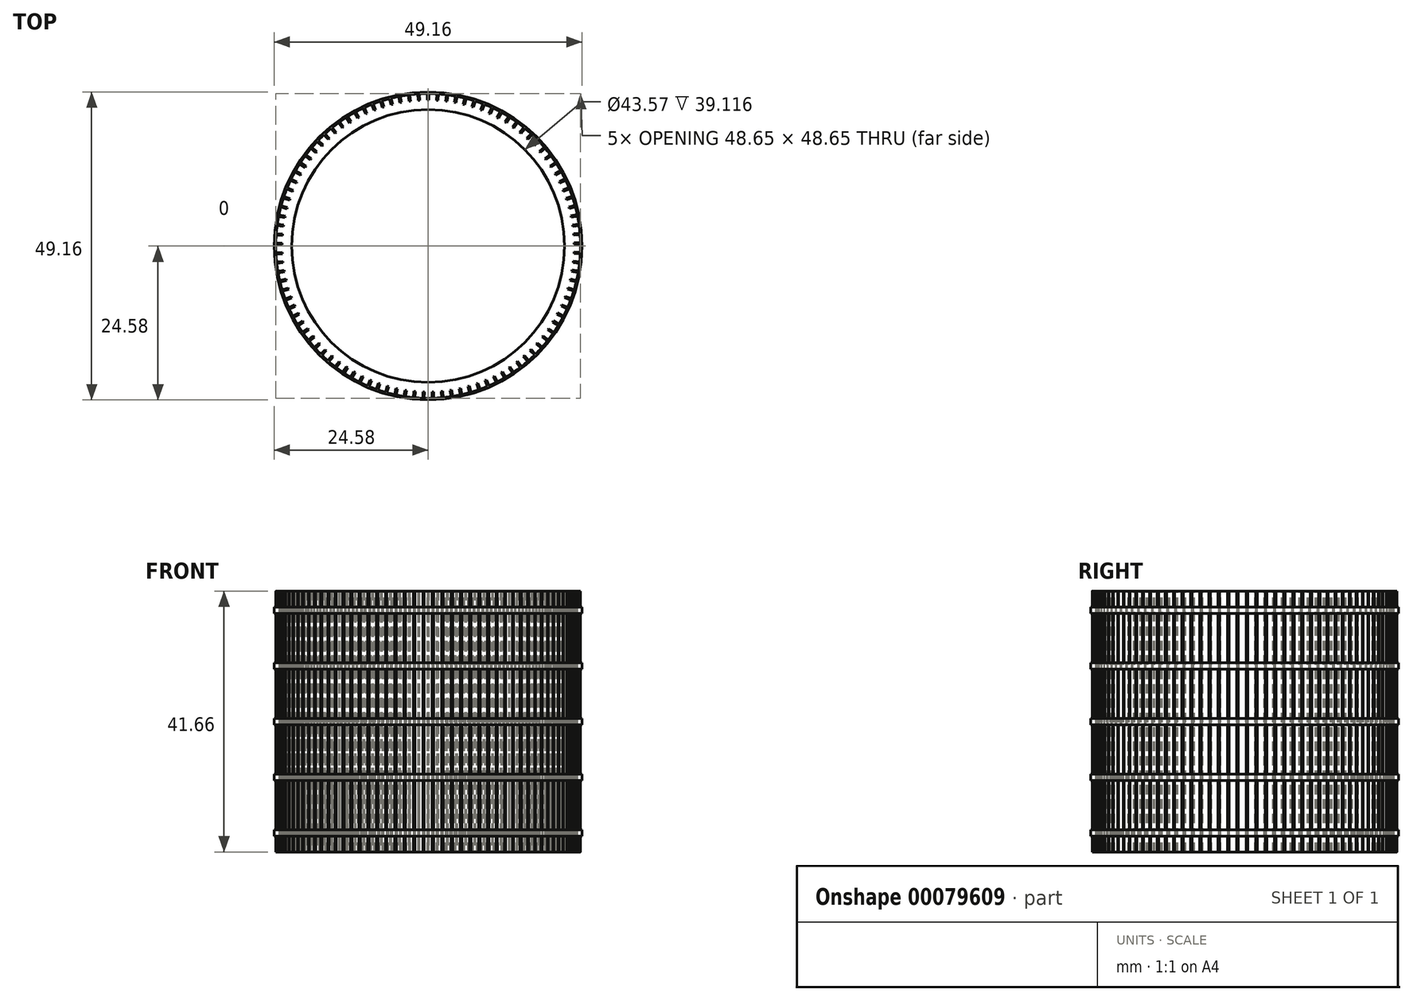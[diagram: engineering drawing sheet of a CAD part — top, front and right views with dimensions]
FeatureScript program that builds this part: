
annotation { "Feature Type Name" : "Feature", "Feature Type Description" : "" }
export const myFeature = defineFeature(function(context is Context, id is Id, definition is map)
    precondition{}
    {
        {
            var Q0;
            Q0=qCreatedBy(makeId("Top.planeOp"),FACE);
            var sketch = newSketch(context, id + "F0", { "sketchPlane" : qUnion([Q0])});
            skCircle(sketch, "E0", {"center": v(0, 0) * mm, "radius": 24.32 * mm});
            skSolve(sketch);
        }
        {
            var Q0;
            Q0=qCreatedBy(makeId("Top.planeOp"),FACE);
            cPlane(context, id + "F1", {"entities" : qUnion([Q0]), "cplaneType" : CPlaneType.OFFSET, "offset" : 2.54 * mm, "width" : 152.4 * mm, "height" : 152.4 * mm});
        }
        {
            var Q0;
            Q0=qCreatedBy(id+"F1.planeOp",FACE);
            cPlane(context, id + "F2", {"entities" : qUnion([Q0]), "cplaneType" : CPlaneType.OFFSET, "offset" : 8.9 * mm, "width" : 152.4 * mm, "height" : 152.4 * mm});
        }
        {
            var Q0;
            Q0=qCreatedBy(id+"F2.planeOp",FACE);
            cPlane(context, id + "F3", {"entities" : qUnion([Q0]), "cplaneType" : CPlaneType.OFFSET, "offset" : 8.9 * mm, "width" : 152.4 * mm, "height" : 152.4 * mm});
        }
        {
            var Q0;
            Q0=qCreatedBy(id+"F3.planeOp",FACE);
            cPlane(context, id + "F4", {"entities" : qUnion([Q0]), "cplaneType" : CPlaneType.OFFSET, "offset" : 8.9 * mm, "width" : 152.4 * mm, "height" : 152.4 * mm});
        }
        {
            var Q0;
            Q0=qSketchRegion(id+"F0",true);
            extrude(context, id + "F5", {"entities" : qUnion([Q0]), "depth" : 41.66 * mm});
        }
        {
            var Q0;
            Q0=makeQuery(id+"F5.opExtrude","CAP_FACE",FACE,{"disambiguationData":[OSD([sQuery(id+"F0.wireOp",EDGE,"E0")])],"isStart":false});
            shell(context, id + "F6", {"entities" : qUnion([Q0]), "thickness" : 2.54 * mm});
        }
        {
            var Q0;
            Q0=makeQuery(id+"F5.opExtrude","CAP_FACE",FACE,{"disambiguationData":[OSD([sQuery(id+"F0.wireOp",EDGE,"E0")])],"isStart":false});
            var sketch = newSketch(context, id + "F7", { "sketchPlane" : qUnion([Q0])});
            skLineSegment(sketch, "E1.left", {"start": v(-0.13, 24.61) * mm, "end": v(-0.13, 23.3) * mm});
            skLineSegment(sketch, "E1.right", {"start": v(0.13, 24.61) * mm, "end": v(0.13, 23.3) * mm});
            skLineSegment(sketch, "E2.1.0", {"start": v(1.4, 24.57) * mm, "end": v(1.32, 23.27) * mm});
            skLineSegment(sketch, "E2.1.1", {"start": v(1.66, 24.56) * mm, "end": v(1.58, 23.25) * mm});
            skLineSegment(sketch, "E2.1.2", {"start": v(1.32, 23.27) * mm, "end": v(1.58, 23.25) * mm});
            skLineSegment(sketch, "E2.1.3", {"start": v(1.4, 24.57) * mm, "end": v(1.66, 24.56) * mm});
            skLineSegment(sketch, "E2.2.0", {"start": v(2.93, 24.44) * mm, "end": v(2.77, 23.14) * mm});
            skLineSegment(sketch, "E2.2.1", {"start": v(3.18, 24.4) * mm, "end": v(3.02, 23.11) * mm});
            skLineSegment(sketch, "E2.2.2", {"start": v(2.77, 23.14) * mm, "end": v(3.02, 23.11) * mm});
            skLineSegment(sketch, "E2.2.3", {"start": v(2.93, 24.44) * mm, "end": v(3.18, 24.4) * mm});
            skLineSegment(sketch, "E2.3.0", {"start": v(4.44, 24.21) * mm, "end": v(4.2, 22.93) * mm});
            skLineSegment(sketch, "E2.3.1", {"start": v(4.7, 24.16) * mm, "end": v(4.45, 22.88) * mm});
            skLineSegment(sketch, "E2.3.2", {"start": v(4.2, 22.93) * mm, "end": v(4.45, 22.88) * mm});
            skLineSegment(sketch, "E2.3.3", {"start": v(4.44, 24.21) * mm, "end": v(4.7, 24.16) * mm});
            skLineSegment(sketch, "E2.4.0", {"start": v(5.94, 23.89) * mm, "end": v(5.62, 22.62) * mm});
            skLineSegment(sketch, "E2.4.1", {"start": v(6.18, 23.83) * mm, "end": v(5.86, 22.56) * mm});
            skLineSegment(sketch, "E2.4.2", {"start": v(5.62, 22.62) * mm, "end": v(5.86, 22.56) * mm});
            skLineSegment(sketch, "E2.4.3", {"start": v(5.94, 23.89) * mm, "end": v(6.18, 23.83) * mm});
            skLineSegment(sketch, "E2.5.0", {"start": v(7.41, 23.47) * mm, "end": v(7.01, 22.23) * mm});
            skLineSegment(sketch, "E2.5.1", {"start": v(7.65, 23.4) * mm, "end": v(7.25, 22.15) * mm});
            skLineSegment(sketch, "E2.5.2", {"start": v(7.01, 22.23) * mm, "end": v(7.25, 22.15) * mm});
            skLineSegment(sketch, "E2.5.3", {"start": v(7.41, 23.47) * mm, "end": v(7.65, 23.4) * mm});
            skLineSegment(sketch, "E2.6.0", {"start": v(8.85, 22.97) * mm, "end": v(8.38, 21.75) * mm});
            skLineSegment(sketch, "E2.6.1", {"start": v(9.1, 22.87) * mm, "end": v(8.61, 21.66) * mm});
            skLineSegment(sketch, "E2.6.2", {"start": v(8.38, 21.75) * mm, "end": v(8.61, 21.66) * mm});
            skLineSegment(sketch, "E2.6.3", {"start": v(8.85, 22.97) * mm, "end": v(9.1, 22.87) * mm});
            skLineSegment(sketch, "E2.7.0", {"start": v(10.27, 22.37) * mm, "end": v(9.71, 21.19) * mm});
            skLineSegment(sketch, "E2.7.1", {"start": v(10.5, 22.26) * mm, "end": v(9.94, 21.08) * mm});
            skLineSegment(sketch, "E2.7.2", {"start": v(9.71, 21.19) * mm, "end": v(9.94, 21.08) * mm});
            skLineSegment(sketch, "E2.7.3", {"start": v(10.27, 22.37) * mm, "end": v(10.5, 22.26) * mm});
            skLineSegment(sketch, "E2.8.0", {"start": v(11.64, 21.7) * mm, "end": v(11.01, 20.54) * mm});
            skLineSegment(sketch, "E2.8.1", {"start": v(11.86, 21.57) * mm, "end": v(11.24, 20.42) * mm});
            skLineSegment(sketch, "E2.8.2", {"start": v(11.01, 20.54) * mm, "end": v(11.24, 20.42) * mm});
            skLineSegment(sketch, "E2.8.3", {"start": v(11.64, 21.7) * mm, "end": v(11.86, 21.57) * mm});
            skLineSegment(sketch, "E2.9.0", {"start": v(12.96, 20.93) * mm, "end": v(12.27, 19.82) * mm});
            skLineSegment(sketch, "E2.9.1", {"start": v(13.18, 20.8) * mm, "end": v(12.48, 19.68) * mm});
            skLineSegment(sketch, "E2.9.2", {"start": v(12.27, 19.82) * mm, "end": v(12.48, 19.68) * mm});
            skLineSegment(sketch, "E2.9.3", {"start": v(12.96, 20.93) * mm, "end": v(13.18, 20.8) * mm});
            skLineSegment(sketch, "E2.10.0", {"start": v(14.24, 20.08) * mm, "end": v(13.48, 19.02) * mm});
            skLineSegment(sketch, "E2.10.1", {"start": v(14.44, 19.93) * mm, "end": v(13.68, 18.87) * mm});
            skLineSegment(sketch, "E2.10.2", {"start": v(13.48, 19.02) * mm, "end": v(13.68, 18.87) * mm});
            skLineSegment(sketch, "E2.10.3", {"start": v(14.24, 20.08) * mm, "end": v(14.44, 19.93) * mm});
            skLineSegment(sketch, "E2.11.0", {"start": v(15.46, 19.16) * mm, "end": v(14.63, 18.14) * mm});
            skLineSegment(sketch, "E2.11.1", {"start": v(15.65, 19) * mm, "end": v(14.83, 17.98) * mm});
            skLineSegment(sketch, "E2.11.2", {"start": v(14.63, 18.14) * mm, "end": v(14.83, 17.98) * mm});
            skLineSegment(sketch, "E2.11.3", {"start": v(15.46, 19.16) * mm, "end": v(15.65, 19) * mm});
            skLineSegment(sketch, "E2.12.0", {"start": v(16.62, 18.16) * mm, "end": v(15.73, 17.2) * mm});
            skLineSegment(sketch, "E2.12.1", {"start": v(16.8, 17.99) * mm, "end": v(15.92, 17.03) * mm});
            skLineSegment(sketch, "E2.12.2", {"start": v(15.73, 17.2) * mm, "end": v(15.92, 17.03) * mm});
            skLineSegment(sketch, "E2.12.3", {"start": v(16.62, 18.16) * mm, "end": v(16.8, 17.99) * mm});
            skLineSegment(sketch, "E2.13.0", {"start": v(17.71, 17.1) * mm, "end": v(16.77, 16.19) * mm});
            skLineSegment(sketch, "E2.13.1", {"start": v(17.9, 16.9) * mm, "end": v(16.94, 16) * mm});
            skLineSegment(sketch, "E2.13.2", {"start": v(16.77, 16.19) * mm, "end": v(16.94, 16) * mm});
            skLineSegment(sketch, "E2.13.3", {"start": v(17.71, 17.1) * mm, "end": v(17.9, 16.9) * mm});
            skLineSegment(sketch, "E2.14.0", {"start": v(18.74, 15.96) * mm, "end": v(17.74, 15.11) * mm});
            skLineSegment(sketch, "E2.14.1", {"start": v(18.9, 15.76) * mm, "end": v(17.9, 14.92) * mm});
            skLineSegment(sketch, "E2.14.2", {"start": v(17.74, 15.11) * mm, "end": v(17.9, 14.92) * mm});
            skLineSegment(sketch, "E2.14.3", {"start": v(18.74, 15.96) * mm, "end": v(18.9, 15.76) * mm});
            skLineSegment(sketch, "E2.15.0", {"start": v(19.7, 14.76) * mm, "end": v(18.65, 13.98) * mm});
            skLineSegment(sketch, "E2.15.1", {"start": v(19.85, 14.56) * mm, "end": v(18.8, 13.78) * mm});
            skLineSegment(sketch, "E2.15.2", {"start": v(18.65, 13.98) * mm, "end": v(18.8, 13.78) * mm});
            skLineSegment(sketch, "E2.15.3", {"start": v(19.7, 14.76) * mm, "end": v(19.85, 14.56) * mm});
            skLineSegment(sketch, "E2.16.0", {"start": v(20.58, 13.5) * mm, "end": v(19.48, 12.8) * mm});
            skLineSegment(sketch, "E2.16.1", {"start": v(20.72, 13.3) * mm, "end": v(19.62, 12.58) * mm});
            skLineSegment(sketch, "E2.16.2", {"start": v(19.48, 12.8) * mm, "end": v(19.62, 12.58) * mm});
            skLineSegment(sketch, "E2.16.3", {"start": v(20.58, 13.5) * mm, "end": v(20.72, 13.3) * mm});
            skLineSegment(sketch, "E2.17.0", {"start": v(21.38, 12.2) * mm, "end": v(20.24, 11.56) * mm});
            skLineSegment(sketch, "E2.17.1", {"start": v(21.5, 11.98) * mm, "end": v(20.36, 11.34) * mm});
            skLineSegment(sketch, "E2.17.2", {"start": v(20.24, 11.56) * mm, "end": v(20.36, 11.34) * mm});
            skLineSegment(sketch, "E2.17.3", {"start": v(21.38, 12.2) * mm, "end": v(21.5, 11.98) * mm});
            skLineSegment(sketch, "E2.18.0", {"start": v(22.1, 10.85) * mm, "end": v(20.92, 10.28) * mm});
            skLineSegment(sketch, "E2.18.1", {"start": v(22.2, 10.62) * mm, "end": v(21.03, 10.05) * mm});
            skLineSegment(sketch, "E2.18.2", {"start": v(20.92, 10.28) * mm, "end": v(21.03, 10.05) * mm});
            skLineSegment(sketch, "E2.18.3", {"start": v(22.1, 10.85) * mm, "end": v(22.2, 10.62) * mm});
            skLineSegment(sketch, "E2.19.0", {"start": v(22.73, 9.46) * mm, "end": v(21.52, 8.96) * mm});
            skLineSegment(sketch, "E2.19.1", {"start": v(22.82, 9.22) * mm, "end": v(21.61, 8.73) * mm});
            skLineSegment(sketch, "E2.19.2", {"start": v(21.52, 8.96) * mm, "end": v(21.61, 8.73) * mm});
            skLineSegment(sketch, "E2.19.3", {"start": v(22.73, 9.46) * mm, "end": v(22.82, 9.22) * mm});
            skLineSegment(sketch, "E2.20.0", {"start": v(23.27, 8.03) * mm, "end": v(22.03, 7.6) * mm});
            skLineSegment(sketch, "E2.20.1", {"start": v(23.35, 7.78) * mm, "end": v(22.11, 7.36) * mm});
            skLineSegment(sketch, "E2.20.2", {"start": v(22.03, 7.6) * mm, "end": v(22.11, 7.36) * mm});
            skLineSegment(sketch, "E2.20.3", {"start": v(23.27, 8.03) * mm, "end": v(23.35, 7.78) * mm});
            skLineSegment(sketch, "E2.21.0", {"start": v(23.72, 6.56) * mm, "end": v(22.46, 6.22) * mm});
            skLineSegment(sketch, "E2.21.1", {"start": v(23.79, 6.32) * mm, "end": v(22.53, 5.98) * mm});
            skLineSegment(sketch, "E2.21.2", {"start": v(22.46, 6.22) * mm, "end": v(22.53, 5.98) * mm});
            skLineSegment(sketch, "E2.21.3", {"start": v(23.72, 6.56) * mm, "end": v(23.79, 6.32) * mm});
            skLineSegment(sketch, "E2.22.0", {"start": v(24.09, 5.08) * mm, "end": v(22.8, 4.81) * mm});
            skLineSegment(sketch, "E2.22.1", {"start": v(24.14, 4.83) * mm, "end": v(22.86, 4.56) * mm});
            skLineSegment(sketch, "E2.22.2", {"start": v(22.8, 4.81) * mm, "end": v(22.86, 4.56) * mm});
            skLineSegment(sketch, "E2.22.3", {"start": v(24.09, 5.08) * mm, "end": v(24.14, 4.83) * mm});
            skLineSegment(sketch, "E2.23.0", {"start": v(24.35, 3.57) * mm, "end": v(23.06, 3.39) * mm});
            skLineSegment(sketch, "E2.23.1", {"start": v(24.39, 3.32) * mm, "end": v(23.1, 3.14) * mm});
            skLineSegment(sketch, "E2.23.2", {"start": v(23.06, 3.39) * mm, "end": v(23.1, 3.14) * mm});
            skLineSegment(sketch, "E2.23.3", {"start": v(24.35, 3.57) * mm, "end": v(24.39, 3.32) * mm});
            skLineSegment(sketch, "E2.24.0", {"start": v(24.53, 2.05) * mm, "end": v(23.23, 1.95) * mm});
            skLineSegment(sketch, "E2.24.1", {"start": v(24.55, 1.8) * mm, "end": v(23.25, 1.7) * mm});
            skLineSegment(sketch, "E2.24.2", {"start": v(23.23, 1.95) * mm, "end": v(23.25, 1.7) * mm});
            skLineSegment(sketch, "E2.24.3", {"start": v(24.53, 2.05) * mm, "end": v(24.55, 1.8) * mm});
            skLineSegment(sketch, "E2.25.0", {"start": v(24.6, 0.52) * mm, "end": v(23.3, 0.5) * mm});
            skLineSegment(sketch, "E2.25.1", {"start": v(24.61, 0.27) * mm, "end": v(23.3, 0.25) * mm});
            skLineSegment(sketch, "E2.25.2", {"start": v(23.3, 0.5) * mm, "end": v(23.3, 0.25) * mm});
            skLineSegment(sketch, "E2.25.3", {"start": v(24.6, 0.52) * mm, "end": v(24.61, 0.27) * mm});
            skLineSegment(sketch, "E2.26.0", {"start": v(24.6, -1.01) * mm, "end": v(23.29, -0.95) * mm});
            skLineSegment(sketch, "E2.26.1", {"start": v(24.58, -1.26) * mm, "end": v(23.28, -1.2) * mm});
            skLineSegment(sketch, "E2.26.2", {"start": v(23.29, -0.95) * mm, "end": v(23.28, -1.2) * mm});
            skLineSegment(sketch, "E2.26.3", {"start": v(24.6, -1.01) * mm, "end": v(24.58, -1.26) * mm});
            skLineSegment(sketch, "E2.27.0", {"start": v(24.48, -2.54) * mm, "end": v(23.18, -2.4) * mm});
            skLineSegment(sketch, "E2.27.1", {"start": v(24.46, -2.79) * mm, "end": v(23.16, -2.65) * mm});
            skLineSegment(sketch, "E2.27.2", {"start": v(23.18, -2.4) * mm, "end": v(23.16, -2.65) * mm});
            skLineSegment(sketch, "E2.27.3", {"start": v(24.48, -2.54) * mm, "end": v(24.46, -2.79) * mm});
            skLineSegment(sketch, "E2.28.0", {"start": v(24.28, -4.05) * mm, "end": v(23, -3.83) * mm});
            skLineSegment(sketch, "E2.28.1", {"start": v(24.24, -4.3) * mm, "end": v(22.95, -4.08) * mm});
            skLineSegment(sketch, "E2.28.2", {"start": v(23, -3.83) * mm, "end": v(22.95, -4.08) * mm});
            skLineSegment(sketch, "E2.28.3", {"start": v(24.28, -4.05) * mm, "end": v(24.24, -4.3) * mm});
            skLineSegment(sketch, "E2.29.0", {"start": v(23.98, -5.55) * mm, "end": v(22.7, -5.25) * mm});
            skLineSegment(sketch, "E2.29.1", {"start": v(23.92, -5.8) * mm, "end": v(22.65, -5.5) * mm});
            skLineSegment(sketch, "E2.29.2", {"start": v(22.7, -5.25) * mm, "end": v(22.65, -5.5) * mm});
            skLineSegment(sketch, "E2.29.3", {"start": v(23.98, -5.55) * mm, "end": v(23.92, -5.8) * mm});
            skLineSegment(sketch, "E2.30.0", {"start": v(23.59, -7.03) * mm, "end": v(22.34, -6.65) * mm});
            skLineSegment(sketch, "E2.30.1", {"start": v(23.51, -7.28) * mm, "end": v(22.26, -6.9) * mm});
            skLineSegment(sketch, "E2.30.2", {"start": v(22.34, -6.65) * mm, "end": v(22.26, -6.9) * mm});
            skLineSegment(sketch, "E2.30.3", {"start": v(23.59, -7.03) * mm, "end": v(23.51, -7.28) * mm});
            skLineSegment(sketch, "E2.31.0", {"start": v(23.1, -8.49) * mm, "end": v(21.88, -8.03) * mm});
            skLineSegment(sketch, "E2.31.1", {"start": v(23.02, -8.72) * mm, "end": v(21.8, -8.27) * mm});
            skLineSegment(sketch, "E2.31.2", {"start": v(21.88, -8.03) * mm, "end": v(21.8, -8.27) * mm});
            skLineSegment(sketch, "E2.31.3", {"start": v(23.1, -8.49) * mm, "end": v(23.02, -8.72) * mm});
            skLineSegment(sketch, "E2.32.0", {"start": v(22.53, -9.9) * mm, "end": v(21.34, -9.37) * mm});
            skLineSegment(sketch, "E2.32.1", {"start": v(22.43, -10.14) * mm, "end": v(21.24, -9.6) * mm});
            skLineSegment(sketch, "E2.32.2", {"start": v(21.34, -9.37) * mm, "end": v(21.24, -9.6) * mm});
            skLineSegment(sketch, "E2.32.3", {"start": v(22.53, -9.9) * mm, "end": v(22.43, -10.14) * mm});
            skLineSegment(sketch, "E2.33.0", {"start": v(21.87, -11.29) * mm, "end": v(20.72, -10.68) * mm});
            skLineSegment(sketch, "E2.33.1", {"start": v(21.76, -11.51) * mm, "end": v(20.6, -10.9) * mm});
            skLineSegment(sketch, "E2.33.2", {"start": v(20.72, -10.68) * mm, "end": v(20.6, -10.9) * mm});
            skLineSegment(sketch, "E2.33.3", {"start": v(21.87, -11.29) * mm, "end": v(21.76, -11.51) * mm});
            skLineSegment(sketch, "E2.34.0", {"start": v(21.13, -12.63) * mm, "end": v(20.01, -11.95) * mm});
            skLineSegment(sketch, "E2.34.1", {"start": v(21, -12.84) * mm, "end": v(19.88, -12.17) * mm});
            skLineSegment(sketch, "E2.34.2", {"start": v(20.01, -11.95) * mm, "end": v(19.88, -12.17) * mm});
            skLineSegment(sketch, "E2.34.3", {"start": v(21.13, -12.63) * mm, "end": v(21, -12.84) * mm});
            skLineSegment(sketch, "E2.35.0", {"start": v(20.3, -13.91) * mm, "end": v(19.23, -13.17) * mm});
            skLineSegment(sketch, "E2.35.1", {"start": v(20.16, -14.12) * mm, "end": v(19.09, -13.38) * mm});
            skLineSegment(sketch, "E2.35.2", {"start": v(19.23, -13.17) * mm, "end": v(19.09, -13.38) * mm});
            skLineSegment(sketch, "E2.35.3", {"start": v(20.3, -13.91) * mm, "end": v(20.16, -14.12) * mm});
            skLineSegment(sketch, "E2.36.0", {"start": v(19.4, -15.15) * mm, "end": v(18.37, -14.34) * mm});
            skLineSegment(sketch, "E2.36.1", {"start": v(19.24, -15.35) * mm, "end": v(18.22, -14.54) * mm});
            skLineSegment(sketch, "E2.36.2", {"start": v(18.37, -14.34) * mm, "end": v(18.22, -14.54) * mm});
            skLineSegment(sketch, "E2.36.3", {"start": v(19.4, -15.15) * mm, "end": v(19.24, -15.35) * mm});
            skLineSegment(sketch, "E2.37.0", {"start": v(18.42, -16.33) * mm, "end": v(17.45, -15.45) * mm});
            skLineSegment(sketch, "E2.37.1", {"start": v(18.25, -16.52) * mm, "end": v(17.28, -15.64) * mm});
            skLineSegment(sketch, "E2.37.2", {"start": v(17.45, -15.45) * mm, "end": v(17.28, -15.64) * mm});
            skLineSegment(sketch, "E2.37.3", {"start": v(18.42, -16.33) * mm, "end": v(18.25, -16.52) * mm});
            skLineSegment(sketch, "E2.38.0", {"start": v(17.37, -17.44) * mm, "end": v(16.45, -16.5) * mm});
            skLineSegment(sketch, "E2.38.1", {"start": v(17.2, -17.62) * mm, "end": v(16.27, -16.69) * mm});
            skLineSegment(sketch, "E2.38.2", {"start": v(16.45, -16.5) * mm, "end": v(16.27, -16.69) * mm});
            skLineSegment(sketch, "E2.38.3", {"start": v(17.37, -17.44) * mm, "end": v(17.2, -17.62) * mm});
            skLineSegment(sketch, "E2.39.0", {"start": v(16.25, -18.49) * mm, "end": v(15.4, -17.5) * mm});
            skLineSegment(sketch, "E2.39.1", {"start": v(16.06, -18.65) * mm, "end": v(15.2, -17.67) * mm});
            skLineSegment(sketch, "E2.39.2", {"start": v(15.4, -17.5) * mm, "end": v(15.2, -17.67) * mm});
            skLineSegment(sketch, "E2.39.3", {"start": v(16.25, -18.49) * mm, "end": v(16.06, -18.65) * mm});
            skLineSegment(sketch, "E2.40.0", {"start": v(15.07, -19.46) * mm, "end": v(14.28, -18.42) * mm});
            skLineSegment(sketch, "E2.40.1", {"start": v(14.87, -19.61) * mm, "end": v(14.08, -18.58) * mm});
            skLineSegment(sketch, "E2.40.2", {"start": v(14.28, -18.42) * mm, "end": v(14.08, -18.58) * mm});
            skLineSegment(sketch, "E2.40.3", {"start": v(15.07, -19.46) * mm, "end": v(14.87, -19.61) * mm});
            skLineSegment(sketch, "E2.41.0", {"start": v(13.83, -20.36) * mm, "end": v(13.1, -19.27) * mm});
            skLineSegment(sketch, "E2.41.1", {"start": v(13.62, -20.5) * mm, "end": v(12.9, -19.42) * mm});
            skLineSegment(sketch, "E2.41.2", {"start": v(13.1, -19.27) * mm, "end": v(12.9, -19.42) * mm});
            skLineSegment(sketch, "E2.41.3", {"start": v(13.83, -20.36) * mm, "end": v(13.62, -20.5) * mm});
            skLineSegment(sketch, "E2.42.0", {"start": v(12.54, -21.18) * mm, "end": v(11.88, -20.05) * mm});
            skLineSegment(sketch, "E2.42.1", {"start": v(12.32, -21.3) * mm, "end": v(11.66, -20.18) * mm});
            skLineSegment(sketch, "E2.42.2", {"start": v(11.88, -20.05) * mm, "end": v(11.66, -20.18) * mm});
            skLineSegment(sketch, "E2.42.3", {"start": v(12.54, -21.18) * mm, "end": v(12.32, -21.3) * mm});
            skLineSegment(sketch, "E2.43.0", {"start": v(11.2, -21.92) * mm, "end": v(10.61, -20.75) * mm});
            skLineSegment(sketch, "E2.43.1", {"start": v(10.98, -22.03) * mm, "end": v(10.39, -20.87) * mm});
            skLineSegment(sketch, "E2.43.2", {"start": v(10.61, -20.75) * mm, "end": v(10.39, -20.87) * mm});
            skLineSegment(sketch, "E2.43.3", {"start": v(11.2, -21.92) * mm, "end": v(10.98, -22.03) * mm});
            skLineSegment(sketch, "E2.44.0", {"start": v(9.82, -22.57) * mm, "end": v(9.3, -21.37) * mm});
            skLineSegment(sketch, "E2.44.1", {"start": v(9.58, -22.67) * mm, "end": v(9.07, -21.47) * mm});
            skLineSegment(sketch, "E2.44.2", {"start": v(9.3, -21.37) * mm, "end": v(9.07, -21.47) * mm});
            skLineSegment(sketch, "E2.44.3", {"start": v(9.82, -22.57) * mm, "end": v(9.58, -22.67) * mm});
            skLineSegment(sketch, "E2.45.0", {"start": v(8.4, -23.14) * mm, "end": v(7.96, -21.9) * mm});
            skLineSegment(sketch, "E2.45.1", {"start": v(8.16, -23.22) * mm, "end": v(7.72, -22) * mm});
            skLineSegment(sketch, "E2.45.2", {"start": v(7.96, -21.9) * mm, "end": v(7.72, -22) * mm});
            skLineSegment(sketch, "E2.45.3", {"start": v(8.4, -23.14) * mm, "end": v(8.16, -23.22) * mm});
            skLineSegment(sketch, "E2.46.0", {"start": v(6.94, -23.62) * mm, "end": v(6.58, -22.36) * mm});
            skLineSegment(sketch, "E2.46.1", {"start": v(6.7, -23.69) * mm, "end": v(6.34, -22.43) * mm});
            skLineSegment(sketch, "E2.46.2", {"start": v(6.58, -22.36) * mm, "end": v(6.34, -22.43) * mm});
            skLineSegment(sketch, "E2.46.3", {"start": v(6.94, -23.62) * mm, "end": v(6.7, -23.69) * mm});
            skLineSegment(sketch, "E2.47.0", {"start": v(5.46, -24) * mm, "end": v(5.18, -22.73) * mm});
            skLineSegment(sketch, "E2.47.1", {"start": v(5.21, -24.06) * mm, "end": v(4.93, -22.78) * mm});
            skLineSegment(sketch, "E2.47.2", {"start": v(5.18, -22.73) * mm, "end": v(4.93, -22.78) * mm});
            skLineSegment(sketch, "E2.47.3", {"start": v(5.46, -24) * mm, "end": v(5.21, -24.06) * mm});
            skLineSegment(sketch, "E2.48.0", {"start": v(3.96, -24.3) * mm, "end": v(3.75, -23) * mm});
            skLineSegment(sketch, "E2.48.1", {"start": v(3.7, -24.33) * mm, "end": v(3.5, -23.04) * mm});
            skLineSegment(sketch, "E2.48.2", {"start": v(3.75, -23) * mm, "end": v(3.5, -23.04) * mm});
            skLineSegment(sketch, "E2.48.3", {"start": v(3.96, -24.3) * mm, "end": v(3.7, -24.33) * mm});
            skLineSegment(sketch, "E2.49.0", {"start": v(2.44, -24.5) * mm, "end": v(2.32, -23.2) * mm});
            skLineSegment(sketch, "E2.49.1", {"start": v(2.19, -24.52) * mm, "end": v(2.06, -23.22) * mm});
            skLineSegment(sketch, "E2.49.2", {"start": v(2.32, -23.2) * mm, "end": v(2.06, -23.22) * mm});
            skLineSegment(sketch, "E2.49.3", {"start": v(2.44, -24.5) * mm, "end": v(2.19, -24.52) * mm});
            skLineSegment(sketch, "E2.50.0", {"start": v(0.91, -24.6) * mm, "end": v(0.87, -23.3) * mm});
            skLineSegment(sketch, "E2.50.1", {"start": v(0.66, -24.6) * mm, "end": v(0.62, -23.3) * mm});
            skLineSegment(sketch, "E2.50.2", {"start": v(0.87, -23.3) * mm, "end": v(0.62, -23.3) * mm});
            skLineSegment(sketch, "E2.50.3", {"start": v(0.91, -24.6) * mm, "end": v(0.66, -24.6) * mm});
            skLineSegment(sketch, "E2.51.0", {"start": v(-0.62, -24.6) * mm, "end": v(-0.58, -23.3) * mm});
            skLineSegment(sketch, "E2.51.1", {"start": v(-0.87, -24.6) * mm, "end": v(-0.83, -23.3) * mm});
            skLineSegment(sketch, "E2.51.2", {"start": v(-0.58, -23.3) * mm, "end": v(-0.83, -23.3) * mm});
            skLineSegment(sketch, "E2.51.3", {"start": v(-0.62, -24.6) * mm, "end": v(-0.87, -24.6) * mm});
            skLineSegment(sketch, "E2.52.0", {"start": v(-2.15, -24.52) * mm, "end": v(-2.02, -23.22) * mm});
            skLineSegment(sketch, "E2.52.1", {"start": v(-2.4, -24.5) * mm, "end": v(-2.28, -23.2) * mm});
            skLineSegment(sketch, "E2.52.2", {"start": v(-2.02, -23.22) * mm, "end": v(-2.28, -23.2) * mm});
            skLineSegment(sketch, "E2.52.3", {"start": v(-2.15, -24.52) * mm, "end": v(-2.4, -24.5) * mm});
            skLineSegment(sketch, "E2.53.0", {"start": v(-3.66, -24.34) * mm, "end": v(-3.46, -23.05) * mm});
            skLineSegment(sketch, "E2.53.1", {"start": v(-3.92, -24.3) * mm, "end": v(-3.71, -23) * mm});
            skLineSegment(sketch, "E2.53.2", {"start": v(-3.46, -23.05) * mm, "end": v(-3.71, -23) * mm});
            skLineSegment(sketch, "E2.53.3", {"start": v(-3.66, -24.34) * mm, "end": v(-3.92, -24.3) * mm});
            skLineSegment(sketch, "E2.54.0", {"start": v(-5.17, -24.07) * mm, "end": v(-4.89, -22.79) * mm});
            skLineSegment(sketch, "E2.54.1", {"start": v(-5.42, -24.01) * mm, "end": v(-5.14, -22.73) * mm});
            skLineSegment(sketch, "E2.54.2", {"start": v(-4.89, -22.79) * mm, "end": v(-5.14, -22.73) * mm});
            skLineSegment(sketch, "E2.54.3", {"start": v(-5.17, -24.07) * mm, "end": v(-5.42, -24.01) * mm});
            skLineSegment(sketch, "E2.55.0", {"start": v(-6.66, -23.7) * mm, "end": v(-6.3, -22.44) * mm});
            skLineSegment(sketch, "E2.55.1", {"start": v(-6.9, -23.63) * mm, "end": v(-6.54, -22.37) * mm});
            skLineSegment(sketch, "E2.55.2", {"start": v(-6.3, -22.44) * mm, "end": v(-6.54, -22.37) * mm});
            skLineSegment(sketch, "E2.55.3", {"start": v(-6.66, -23.7) * mm, "end": v(-6.9, -23.63) * mm});
            skLineSegment(sketch, "E2.56.0", {"start": v(-8.12, -23.24) * mm, "end": v(-7.68, -22) * mm});
            skLineSegment(sketch, "E2.56.1", {"start": v(-8.36, -23.15) * mm, "end": v(-7.92, -21.92) * mm});
            skLineSegment(sketch, "E2.56.2", {"start": v(-7.68, -22) * mm, "end": v(-7.92, -21.92) * mm});
            skLineSegment(sketch, "E2.56.3", {"start": v(-8.12, -23.24) * mm, "end": v(-8.36, -23.15) * mm});
            skLineSegment(sketch, "E2.57.0", {"start": v(-9.54, -22.69) * mm, "end": v(-9.03, -21.49) * mm});
            skLineSegment(sketch, "E2.57.1", {"start": v(-9.78, -22.59) * mm, "end": v(-9.27, -21.39) * mm});
            skLineSegment(sketch, "E2.57.2", {"start": v(-9.03, -21.49) * mm, "end": v(-9.27, -21.39) * mm});
            skLineSegment(sketch, "E2.57.3", {"start": v(-9.54, -22.69) * mm, "end": v(-9.78, -22.59) * mm});
            skLineSegment(sketch, "E2.58.0", {"start": v(-10.94, -22.05) * mm, "end": v(-10.35, -20.88) * mm});
            skLineSegment(sketch, "E2.58.1", {"start": v(-11.16, -21.94) * mm, "end": v(-10.58, -20.77) * mm});
            skLineSegment(sketch, "E2.58.2", {"start": v(-10.35, -20.88) * mm, "end": v(-10.58, -20.77) * mm});
            skLineSegment(sketch, "E2.58.3", {"start": v(-10.94, -22.05) * mm, "end": v(-11.16, -21.94) * mm});
            skLineSegment(sketch, "E2.59.0", {"start": v(-12.29, -21.33) * mm, "end": v(-11.63, -20.2) * mm});
            skLineSegment(sketch, "E2.59.1", {"start": v(-12.5, -21.2) * mm, "end": v(-11.85, -20.07) * mm});
            skLineSegment(sketch, "E2.59.2", {"start": v(-11.63, -20.2) * mm, "end": v(-11.85, -20.07) * mm});
            skLineSegment(sketch, "E2.59.3", {"start": v(-12.29, -21.33) * mm, "end": v(-12.5, -21.2) * mm});
            skLineSegment(sketch, "E2.60.0", {"start": v(-13.59, -20.52) * mm, "end": v(-12.86, -19.44) * mm});
            skLineSegment(sketch, "E2.60.1", {"start": v(-13.8, -20.38) * mm, "end": v(-13.07, -19.3) * mm});
            skLineSegment(sketch, "E2.60.2", {"start": v(-12.86, -19.44) * mm, "end": v(-13.07, -19.3) * mm});
            skLineSegment(sketch, "E2.60.3", {"start": v(-13.59, -20.52) * mm, "end": v(-13.8, -20.38) * mm});
            skLineSegment(sketch, "E2.61.0", {"start": v(-14.84, -19.64) * mm, "end": v(-14.04, -18.6) * mm});
            skLineSegment(sketch, "E2.61.1", {"start": v(-15.04, -19.49) * mm, "end": v(-14.25, -18.45) * mm});
            skLineSegment(sketch, "E2.61.2", {"start": v(-14.04, -18.6) * mm, "end": v(-14.25, -18.45) * mm});
            skLineSegment(sketch, "E2.61.3", {"start": v(-14.84, -19.64) * mm, "end": v(-15.04, -19.49) * mm});
            skLineSegment(sketch, "E2.62.0", {"start": v(-16.03, -18.68) * mm, "end": v(-15.17, -17.7) * mm});
            skLineSegment(sketch, "E2.62.1", {"start": v(-16.22, -18.51) * mm, "end": v(-15.36, -17.53) * mm});
            skLineSegment(sketch, "E2.62.2", {"start": v(-15.17, -17.7) * mm, "end": v(-15.36, -17.53) * mm});
            skLineSegment(sketch, "E2.62.3", {"start": v(-16.03, -18.68) * mm, "end": v(-16.22, -18.51) * mm});
            skLineSegment(sketch, "E2.63.0", {"start": v(-17.16, -17.65) * mm, "end": v(-16.24, -16.72) * mm});
            skLineSegment(sketch, "E2.63.1", {"start": v(-17.34, -17.47) * mm, "end": v(-16.42, -16.54) * mm});
            skLineSegment(sketch, "E2.63.2", {"start": v(-16.24, -16.72) * mm, "end": v(-16.42, -16.54) * mm});
            skLineSegment(sketch, "E2.63.3", {"start": v(-17.16, -17.65) * mm, "end": v(-17.34, -17.47) * mm});
            skLineSegment(sketch, "E2.64.0", {"start": v(-18.22, -16.55) * mm, "end": v(-17.25, -15.67) * mm});
            skLineSegment(sketch, "E2.64.1", {"start": v(-18.4, -16.36) * mm, "end": v(-17.42, -15.48) * mm});
            skLineSegment(sketch, "E2.64.2", {"start": v(-17.25, -15.67) * mm, "end": v(-17.42, -15.48) * mm});
            skLineSegment(sketch, "E2.64.3", {"start": v(-18.22, -16.55) * mm, "end": v(-18.4, -16.36) * mm});
            skLineSegment(sketch, "E2.65.0", {"start": v(-19.22, -15.38) * mm, "end": v(-18.2, -14.57) * mm});
            skLineSegment(sketch, "E2.65.1", {"start": v(-19.37, -15.18) * mm, "end": v(-18.35, -14.37) * mm});
            skLineSegment(sketch, "E2.65.2", {"start": v(-18.2, -14.57) * mm, "end": v(-18.35, -14.37) * mm});
            skLineSegment(sketch, "E2.65.3", {"start": v(-19.22, -15.38) * mm, "end": v(-19.37, -15.18) * mm});
            skLineSegment(sketch, "E2.66.0", {"start": v(-20.14, -14.16) * mm, "end": v(-19.06, -13.41) * mm});
            skLineSegment(sketch, "E2.66.1", {"start": v(-20.28, -13.95) * mm, "end": v(-19.2, -13.2) * mm});
            skLineSegment(sketch, "E2.66.2", {"start": v(-19.06, -13.41) * mm, "end": v(-19.2, -13.2) * mm});
            skLineSegment(sketch, "E2.66.3", {"start": v(-20.14, -14.16) * mm, "end": v(-20.28, -13.95) * mm});
            skLineSegment(sketch, "E2.67.0", {"start": v(-20.98, -12.88) * mm, "end": v(-19.86, -12.2) * mm});
            skLineSegment(sketch, "E2.67.1", {"start": v(-21.1, -12.66) * mm, "end": v(-20, -11.98) * mm});
            skLineSegment(sketch, "E2.67.2", {"start": v(-19.86, -12.2) * mm, "end": v(-20, -11.98) * mm});
            skLineSegment(sketch, "E2.67.3", {"start": v(-20.98, -12.88) * mm, "end": v(-21.1, -12.66) * mm});
            skLineSegment(sketch, "E2.68.0", {"start": v(-21.74, -11.55) * mm, "end": v(-20.58, -10.94) * mm});
            skLineSegment(sketch, "E2.68.1", {"start": v(-21.85, -11.33) * mm, "end": v(-20.7, -10.72) * mm});
            skLineSegment(sketch, "E2.68.2", {"start": v(-20.58, -10.94) * mm, "end": v(-20.7, -10.72) * mm});
            skLineSegment(sketch, "E2.68.3", {"start": v(-21.74, -11.55) * mm, "end": v(-21.85, -11.33) * mm});
            skLineSegment(sketch, "E2.69.0", {"start": v(-22.41, -10.18) * mm, "end": v(-21.22, -9.64) * mm});
            skLineSegment(sketch, "E2.69.1", {"start": v(-22.52, -9.95) * mm, "end": v(-21.32, -9.41) * mm});
            skLineSegment(sketch, "E2.69.2", {"start": v(-21.22, -9.64) * mm, "end": v(-21.32, -9.41) * mm});
            skLineSegment(sketch, "E2.69.3", {"start": v(-22.41, -10.18) * mm, "end": v(-22.52, -9.95) * mm});
            skLineSegment(sketch, "E2.70.0", {"start": v(-23, -8.76) * mm, "end": v(-21.78, -8.3) * mm});
            skLineSegment(sketch, "E2.70.1", {"start": v(-23.1, -8.53) * mm, "end": v(-21.87, -8.07) * mm});
            skLineSegment(sketch, "E2.70.2", {"start": v(-21.78, -8.3) * mm, "end": v(-21.87, -8.07) * mm});
            skLineSegment(sketch, "E2.70.3", {"start": v(-23, -8.76) * mm, "end": v(-23.1, -8.53) * mm});
            skLineSegment(sketch, "E2.71.0", {"start": v(-23.5, -7.32) * mm, "end": v(-22.25, -6.94) * mm});
            skLineSegment(sketch, "E2.71.1", {"start": v(-23.58, -7.08) * mm, "end": v(-22.33, -6.7) * mm});
            skLineSegment(sketch, "E2.71.2", {"start": v(-22.25, -6.94) * mm, "end": v(-22.33, -6.7) * mm});
            skLineSegment(sketch, "E2.71.3", {"start": v(-23.5, -7.32) * mm, "end": v(-23.58, -7.08) * mm});
            skLineSegment(sketch, "E2.72.0", {"start": v(-23.91, -5.84) * mm, "end": v(-22.64, -5.54) * mm});
            skLineSegment(sketch, "E2.72.1", {"start": v(-23.97, -5.6) * mm, "end": v(-22.7, -5.3) * mm});
            skLineSegment(sketch, "E2.72.2", {"start": v(-22.64, -5.54) * mm, "end": v(-22.7, -5.3) * mm});
            skLineSegment(sketch, "E2.72.3", {"start": v(-23.91, -5.84) * mm, "end": v(-23.97, -5.6) * mm});
            skLineSegment(sketch, "E2.73.0", {"start": v(-24.23, -4.35) * mm, "end": v(-22.94, -4.12) * mm});
            skLineSegment(sketch, "E2.73.1", {"start": v(-24.27, -4.1) * mm, "end": v(-22.98, -3.87) * mm});
            skLineSegment(sketch, "E2.73.2", {"start": v(-22.94, -4.12) * mm, "end": v(-22.98, -3.87) * mm});
            skLineSegment(sketch, "E2.73.3", {"start": v(-24.23, -4.35) * mm, "end": v(-24.27, -4.1) * mm});
            skLineSegment(sketch, "E2.74.0", {"start": v(-24.45, -2.83) * mm, "end": v(-23.15, -2.69) * mm});
            skLineSegment(sketch, "E2.74.1", {"start": v(-24.48, -2.58) * mm, "end": v(-23.18, -2.44) * mm});
            skLineSegment(sketch, "E2.74.2", {"start": v(-23.15, -2.69) * mm, "end": v(-23.18, -2.44) * mm});
            skLineSegment(sketch, "E2.74.3", {"start": v(-24.45, -2.83) * mm, "end": v(-24.48, -2.58) * mm});
            skLineSegment(sketch, "E2.75.0", {"start": v(-24.58, -1.3) * mm, "end": v(-23.27, -1.24) * mm});
            skLineSegment(sketch, "E2.75.1", {"start": v(-24.6, -1.05) * mm, "end": v(-23.29, -1) * mm});
            skLineSegment(sketch, "E2.75.2", {"start": v(-23.27, -1.24) * mm, "end": v(-23.29, -1) * mm});
            skLineSegment(sketch, "E2.75.3", {"start": v(-24.58, -1.3) * mm, "end": v(-24.6, -1.05) * mm});
            skLineSegment(sketch, "E2.76.0", {"start": v(-24.61, 0.22) * mm, "end": v(-23.3, 0.2) * mm});
            skLineSegment(sketch, "E2.76.1", {"start": v(-24.6, 0.48) * mm, "end": v(-23.3, 0.46) * mm});
            skLineSegment(sketch, "E2.76.2", {"start": v(-23.3, 0.2) * mm, "end": v(-23.3, 0.46) * mm});
            skLineSegment(sketch, "E2.76.3", {"start": v(-24.61, 0.22) * mm, "end": v(-24.6, 0.48) * mm});
            skLineSegment(sketch, "E2.77.0", {"start": v(-24.55, 1.75) * mm, "end": v(-23.25, 1.65) * mm});
            skLineSegment(sketch, "E2.77.1", {"start": v(-24.53, 2) * mm, "end": v(-23.23, 1.9) * mm});
            skLineSegment(sketch, "E2.77.2", {"start": v(-23.25, 1.65) * mm, "end": v(-23.23, 1.9) * mm});
            skLineSegment(sketch, "E2.77.3", {"start": v(-24.55, 1.75) * mm, "end": v(-24.53, 2) * mm});
            skLineSegment(sketch, "E2.78.0", {"start": v(-24.4, 3.28) * mm, "end": v(-23.1, 3.1) * mm});
            skLineSegment(sketch, "E2.78.1", {"start": v(-24.36, 3.53) * mm, "end": v(-23.07, 3.35) * mm});
            skLineSegment(sketch, "E2.78.2", {"start": v(-23.1, 3.1) * mm, "end": v(-23.07, 3.35) * mm});
            skLineSegment(sketch, "E2.78.3", {"start": v(-24.4, 3.28) * mm, "end": v(-24.36, 3.53) * mm});
            skLineSegment(sketch, "E2.79.0", {"start": v(-24.14, 4.79) * mm, "end": v(-22.86, 4.52) * mm});
            skLineSegment(sketch, "E2.79.1", {"start": v(-24.1, 5.03) * mm, "end": v(-22.81, 4.77) * mm});
            skLineSegment(sketch, "E2.79.2", {"start": v(-22.86, 4.52) * mm, "end": v(-22.81, 4.77) * mm});
            skLineSegment(sketch, "E2.79.3", {"start": v(-24.14, 4.79) * mm, "end": v(-24.1, 5.03) * mm});
            skLineSegment(sketch, "E2.80.0", {"start": v(-23.8, 6.28) * mm, "end": v(-22.54, 5.94) * mm});
            skLineSegment(sketch, "E2.80.1", {"start": v(-23.73, 6.52) * mm, "end": v(-22.47, 6.18) * mm});
            skLineSegment(sketch, "E2.80.2", {"start": v(-22.54, 5.94) * mm, "end": v(-22.47, 6.18) * mm});
            skLineSegment(sketch, "E2.80.3", {"start": v(-23.8, 6.28) * mm, "end": v(-23.73, 6.52) * mm});
            skLineSegment(sketch, "E2.81.0", {"start": v(-23.36, 7.74) * mm, "end": v(-22.13, 7.33) * mm});
            skLineSegment(sketch, "E2.81.1", {"start": v(-23.28, 7.98) * mm, "end": v(-22.04, 7.57) * mm});
            skLineSegment(sketch, "E2.81.2", {"start": v(-22.13, 7.33) * mm, "end": v(-22.04, 7.57) * mm});
            skLineSegment(sketch, "E2.81.3", {"start": v(-23.36, 7.74) * mm, "end": v(-23.28, 7.98) * mm});
            skLineSegment(sketch, "E2.82.0", {"start": v(-22.84, 9.18) * mm, "end": v(-21.63, 8.69) * mm});
            skLineSegment(sketch, "E2.82.1", {"start": v(-22.74, 9.42) * mm, "end": v(-21.53, 8.92) * mm});
            skLineSegment(sketch, "E2.82.2", {"start": v(-21.63, 8.69) * mm, "end": v(-21.53, 8.92) * mm});
            skLineSegment(sketch, "E2.82.3", {"start": v(-22.84, 9.18) * mm, "end": v(-22.74, 9.42) * mm});
            skLineSegment(sketch, "E2.83.0", {"start": v(-22.22, 10.58) * mm, "end": v(-21.05, 10.01) * mm});
            skLineSegment(sketch, "E2.83.1", {"start": v(-22.11, 10.81) * mm, "end": v(-20.94, 10.24) * mm});
            skLineSegment(sketch, "E2.83.2", {"start": v(-21.05, 10.01) * mm, "end": v(-20.94, 10.24) * mm});
            skLineSegment(sketch, "E2.83.3", {"start": v(-22.22, 10.58) * mm, "end": v(-22.11, 10.81) * mm});
            skLineSegment(sketch, "E2.84.0", {"start": v(-21.52, 11.94) * mm, "end": v(-20.38, 11.3) * mm});
            skLineSegment(sketch, "E2.84.1", {"start": v(-21.4, 12.17) * mm, "end": v(-20.26, 11.52) * mm});
            skLineSegment(sketch, "E2.84.2", {"start": v(-20.38, 11.3) * mm, "end": v(-20.26, 11.52) * mm});
            skLineSegment(sketch, "E2.84.3", {"start": v(-21.52, 11.94) * mm, "end": v(-21.4, 12.17) * mm});
            skLineSegment(sketch, "E2.85.0", {"start": v(-20.74, 13.26) * mm, "end": v(-19.64, 12.55) * mm});
            skLineSegment(sketch, "E2.85.1", {"start": v(-20.6, 13.47) * mm, "end": v(-19.5, 12.76) * mm});
            skLineSegment(sketch, "E2.85.2", {"start": v(-19.64, 12.55) * mm, "end": v(-19.5, 12.76) * mm});
            skLineSegment(sketch, "E2.85.3", {"start": v(-20.74, 13.26) * mm, "end": v(-20.6, 13.47) * mm});
            skLineSegment(sketch, "E2.86.0", {"start": v(-19.87, 14.52) * mm, "end": v(-18.82, 13.74) * mm});
            skLineSegment(sketch, "E2.86.1", {"start": v(-19.72, 14.73) * mm, "end": v(-18.67, 13.95) * mm});
            skLineSegment(sketch, "E2.86.2", {"start": v(-18.82, 13.74) * mm, "end": v(-18.67, 13.95) * mm});
            skLineSegment(sketch, "E2.86.3", {"start": v(-19.87, 14.52) * mm, "end": v(-19.72, 14.73) * mm});
            skLineSegment(sketch, "E2.87.0", {"start": v(-18.93, 15.73) * mm, "end": v(-17.93, 14.89) * mm});
            skLineSegment(sketch, "E2.87.1", {"start": v(-18.77, 15.92) * mm, "end": v(-17.77, 15.08) * mm});
            skLineSegment(sketch, "E2.87.2", {"start": v(-17.93, 14.89) * mm, "end": v(-17.77, 15.08) * mm});
            skLineSegment(sketch, "E2.87.3", {"start": v(-18.93, 15.73) * mm, "end": v(-18.77, 15.92) * mm});
            skLineSegment(sketch, "E2.88.0", {"start": v(-17.92, 16.88) * mm, "end": v(-16.97, 15.97) * mm});
            skLineSegment(sketch, "E2.88.1", {"start": v(-17.74, 17.06) * mm, "end": v(-16.8, 16.16) * mm});
            skLineSegment(sketch, "E2.88.2", {"start": v(-16.97, 15.97) * mm, "end": v(-16.8, 16.16) * mm});
            skLineSegment(sketch, "E2.88.3", {"start": v(-17.92, 16.88) * mm, "end": v(-17.74, 17.06) * mm});
            skLineSegment(sketch, "E2.89.0", {"start": v(-16.84, 17.96) * mm, "end": v(-15.95, 17) * mm});
            skLineSegment(sketch, "E2.89.1", {"start": v(-16.65, 18.13) * mm, "end": v(-15.76, 17.17) * mm});
            skLineSegment(sketch, "E2.89.2", {"start": v(-15.95, 17) * mm, "end": v(-15.76, 17.17) * mm});
            skLineSegment(sketch, "E2.89.3", {"start": v(-16.84, 17.96) * mm, "end": v(-16.65, 18.13) * mm});
            skLineSegment(sketch, "E2.90.0", {"start": v(-15.69, 18.97) * mm, "end": v(-14.86, 17.96) * mm});
            skLineSegment(sketch, "E2.90.1", {"start": v(-15.5, 19.13) * mm, "end": v(-14.66, 18.12) * mm});
            skLineSegment(sketch, "E2.90.2", {"start": v(-14.86, 17.96) * mm, "end": v(-14.66, 18.12) * mm});
            skLineSegment(sketch, "E2.90.3", {"start": v(-15.69, 18.97) * mm, "end": v(-15.5, 19.13) * mm});
            skLineSegment(sketch, "E2.91.0", {"start": v(-14.48, 19.9) * mm, "end": v(-13.71, 18.85) * mm});
            skLineSegment(sketch, "E2.91.1", {"start": v(-14.27, 20.05) * mm, "end": v(-13.5, 19) * mm});
            skLineSegment(sketch, "E2.91.2", {"start": v(-13.71, 18.85) * mm, "end": v(-13.5, 19) * mm});
            skLineSegment(sketch, "E2.91.3", {"start": v(-14.48, 19.9) * mm, "end": v(-14.27, 20.05) * mm});
            skLineSegment(sketch, "E2.92.0", {"start": v(-13.21, 20.77) * mm, "end": v(-12.52, 19.66) * mm});
            skLineSegment(sketch, "E2.92.1", {"start": v(-13, 20.9) * mm, "end": v(-12.3, 19.8) * mm});
            skLineSegment(sketch, "E2.92.2", {"start": v(-12.52, 19.66) * mm, "end": v(-12.3, 19.8) * mm});
            skLineSegment(sketch, "E2.92.3", {"start": v(-13.21, 20.77) * mm, "end": v(-13, 20.9) * mm});
            skLineSegment(sketch, "E2.93.0", {"start": v(-11.9, 21.55) * mm, "end": v(-11.27, 20.4) * mm});
            skLineSegment(sketch, "E2.93.1", {"start": v(-11.67, 21.67) * mm, "end": v(-11.05, 20.52) * mm});
            skLineSegment(sketch, "E2.93.2", {"start": v(-11.27, 20.4) * mm, "end": v(-11.05, 20.52) * mm});
            skLineSegment(sketch, "E2.93.3", {"start": v(-11.9, 21.55) * mm, "end": v(-11.67, 21.67) * mm});
            skLineSegment(sketch, "E2.94.0", {"start": v(-10.53, 22.25) * mm, "end": v(-9.98, 21.06) * mm});
            skLineSegment(sketch, "E2.94.1", {"start": v(-10.3, 22.35) * mm, "end": v(-9.75, 21.17) * mm});
            skLineSegment(sketch, "E2.94.2", {"start": v(-9.98, 21.06) * mm, "end": v(-9.75, 21.17) * mm});
            skLineSegment(sketch, "E2.94.3", {"start": v(-10.53, 22.25) * mm, "end": v(-10.3, 22.35) * mm});
            skLineSegment(sketch, "E2.95.0", {"start": v(-9.13, 22.86) * mm, "end": v(-8.65, 21.64) * mm});
            skLineSegment(sketch, "E2.95.1", {"start": v(-8.9, 22.95) * mm, "end": v(-8.42, 21.73) * mm});
            skLineSegment(sketch, "E2.95.2", {"start": v(-8.65, 21.64) * mm, "end": v(-8.42, 21.73) * mm});
            skLineSegment(sketch, "E2.95.3", {"start": v(-9.13, 22.86) * mm, "end": v(-8.9, 22.95) * mm});
            skLineSegment(sketch, "E2.96.0", {"start": v(-7.7, 23.38) * mm, "end": v(-7.3, 22.14) * mm});
            skLineSegment(sketch, "E2.96.1", {"start": v(-7.45, 23.46) * mm, "end": v(-7.05, 22.22) * mm});
            skLineSegment(sketch, "E2.96.2", {"start": v(-7.3, 22.14) * mm, "end": v(-7.05, 22.22) * mm});
            skLineSegment(sketch, "E2.96.3", {"start": v(-7.7, 23.38) * mm, "end": v(-7.45, 23.46) * mm});
            skLineSegment(sketch, "E2.97.0", {"start": v(-6.22, 23.81) * mm, "end": v(-5.9, 22.55) * mm});
            skLineSegment(sketch, "E2.97.1", {"start": v(-5.98, 23.88) * mm, "end": v(-5.65, 22.61) * mm});
            skLineSegment(sketch, "E2.97.2", {"start": v(-5.9, 22.55) * mm, "end": v(-5.65, 22.61) * mm});
            skLineSegment(sketch, "E2.97.3", {"start": v(-6.22, 23.81) * mm, "end": v(-5.98, 23.88) * mm});
            skLineSegment(sketch, "E2.98.0", {"start": v(-4.73, 24.16) * mm, "end": v(-4.49, 22.87) * mm});
            skLineSegment(sketch, "E2.98.1", {"start": v(-4.48, 24.2) * mm, "end": v(-4.24, 22.92) * mm});
            skLineSegment(sketch, "E2.98.2", {"start": v(-4.49, 22.87) * mm, "end": v(-4.24, 22.92) * mm});
            skLineSegment(sketch, "E2.98.3", {"start": v(-4.73, 24.16) * mm, "end": v(-4.48, 24.2) * mm});
            skLineSegment(sketch, "E2.99.0", {"start": v(-3.22, 24.4) * mm, "end": v(-3.06, 23.1) * mm});
            skLineSegment(sketch, "E2.99.1", {"start": v(-2.97, 24.43) * mm, "end": v(-2.8, 23.14) * mm});
            skLineSegment(sketch, "E2.99.2", {"start": v(-3.06, 23.1) * mm, "end": v(-2.8, 23.14) * mm});
            skLineSegment(sketch, "E2.99.3", {"start": v(-3.22, 24.4) * mm, "end": v(-2.97, 24.43) * mm});
            skLineSegment(sketch, "E2.100.0", {"start": v(-1.7, 24.56) * mm, "end": v(-1.62, 23.25) * mm});
            skLineSegment(sketch, "E2.100.1", {"start": v(-1.45, 24.57) * mm, "end": v(-1.36, 23.27) * mm});
            skLineSegment(sketch, "E2.100.2", {"start": v(-1.62, 23.25) * mm, "end": v(-1.36, 23.27) * mm});
            skLineSegment(sketch, "E2.100.3", {"start": v(-1.7, 24.56) * mm, "end": v(-1.45, 24.57) * mm});
            skPoint(sketch, "E2.center", {"position": v(0, 0) * mm});
            skLineSegment(sketch, "E2.anchor1", {"start": v(0, 0) * mm, "end": v(-0.13, 23.3) * mm, "construction": true});
            skLineSegment(sketch, "E2.anchor2", {"start": v(0, 0) * mm, "end": v(-0.17, 23.3) * mm, "construction": true});
            skPoint(sketch, "E3.orphan", {"position": v(0.09, 23.3) * mm});
            skPoint(sketch, "E4.orphan", {"position": v(-0.17, 24.61) * mm});
            skLineSegment(sketch, "E5", {"start": v(-0.13, 23.3) * mm, "end": v(0.13, 23.3) * mm});
            skLineSegment(sketch, "E6", {"start": v(-0.13, 24.61) * mm, "end": v(0.13, 24.61) * mm});
            skSolve(sketch);
        }
        {
            var Q0;
            Q0=qSketchRegion(id+"F7",true);
            extrude(context, id + "F8", {"entities" : qUnion([Q0]), "operationType" : NewBodyOperationType.REMOVE, "endBound" : BoundingType.THROUGH_ALL, "oppositeDirection" : true, "depth" : 25.4 * mm});
        }
        {
            var Q0;
            Q0=qCreatedBy(id+"F4.planeOp",FACE);
            cPlane(context, id + "F9", {"entities" : qUnion([Q0]), "cplaneType" : CPlaneType.OFFSET, "offset" : 8.9 * mm, "width" : 152.4 * mm, "height" : 152.4 * mm});
        }
        {
            var Q0;
            Q0=qCreatedBy(id+"F1.planeOp",FACE);
            var sketch = newSketch(context, id + "F10", { "sketchPlane" : qUnion([Q0])});
            skCircle(sketch, "E7", {"center": v(0, 0) * mm, "radius": 24.58 * mm});
            skCircle(sketch, "E8", {"center": v(0, 0) * mm, "radius": 23.82 * mm});
            skSolve(sketch);
        }
        {
            var Q0;
            Q0=qSketchRegion(id+"F10",true);
            extrude(context, id + "F11", {"entities" : qUnion([Q0]), "operationType" : NewBodyOperationType.ADD, "depth" : 1.02 * mm});
        }
        {
            var Q0;
            Q0=qCreatedBy(id+"F2.planeOp",FACE);
            var sketch = newSketch(context, id + "F12", { "sketchPlane" : qUnion([Q0])});
            skCircle(sketch, "E9", {"center": v(0, 0) * mm, "radius": 24.58 * mm});
            skCircle(sketch, "E10", {"center": v(0, 0) * mm, "radius": 23.82 * mm});
            skSolve(sketch);
        }
        {
            var Q0;
            Q0=qSketchRegion(id+"F12",true);
            var Q1;
            Q1=sQuery(id+"F12.wireOp",EDGE,"E9");
            var Q2;
            Q2=sQuery(id+"F12.wireOp",EDGE,"E10");
            extrude(context, id + "F13", {"entities" : qUnion([Q0]), "operationType" : NewBodyOperationType.ADD, "surfaceEntities" : qUnion([Q1, Q2]), "depth" : 1.02 * mm});
        }
        {
            var Q0;
            Q0=qCreatedBy(id+"F3.planeOp",FACE);
            var sketch = newSketch(context, id + "F14", { "sketchPlane" : qUnion([Q0])});
            skCircle(sketch, "E11", {"center": v(0, 0) * mm, "radius": 24.58 * mm});
            skCircle(sketch, "E12", {"center": v(0, 0) * mm, "radius": 23.82 * mm});
            skSolve(sketch);
        }
        {
            var Q0;
            Q0=qSketchRegion(id+"F14",true);
            extrude(context, id + "F15", {"entities" : qUnion([Q0]), "operationType" : NewBodyOperationType.ADD, "depth" : 1.02 * mm});
        }
        {
            var Q0;
            Q0=qCreatedBy(id+"F4.planeOp",FACE);
            var sketch = newSketch(context, id + "F16", { "sketchPlane" : qUnion([Q0])});
            skCircle(sketch, "E13", {"center": v(0, 0) * mm, "radius": 24.58 * mm});
            skCircle(sketch, "E14", {"center": v(0, 0) * mm, "radius": 23.82 * mm});
            skSolve(sketch);
        }
        {
            var Q0;
            Q0=qSketchRegion(id+"F16",true);
            var Q1;
            Q1=sQuery(id+"F16.wireOp",EDGE,"E13");
            var Q2;
            Q2=sQuery(id+"F16.wireOp",EDGE,"E14");
            extrude(context, id + "F17", {"entities" : qUnion([Q0]), "operationType" : NewBodyOperationType.ADD, "surfaceEntities" : qUnion([Q1, Q2]), "depth" : 1.02 * mm});
        }
        {
            var Q0;
            Q0=qCreatedBy(id+"F9.planeOp",FACE);
            var sketch = newSketch(context, id + "F18", { "sketchPlane" : qUnion([Q0])});
            skCircle(sketch, "E15", {"center": v(0, 0) * mm, "radius": 24.58 * mm});
            skCircle(sketch, "E16", {"center": v(0, 0) * mm, "radius": 23.82 * mm});
            skSolve(sketch);
        }
        {
            var Q0;
            Q0=qSketchRegion(id+"F18",true);
            var Q1;
            Q1=sQuery(id+"F18.wireOp",EDGE,"E15");
            var Q2;
            Q2=sQuery(id+"F18.wireOp",EDGE,"E16");
            extrude(context, id + "F19", {"entities" : qUnion([Q0]), "operationType" : NewBodyOperationType.ADD, "surfaceEntities" : qUnion([Q1, Q2]), "depth" : 1.02 * mm});
        }
    });
